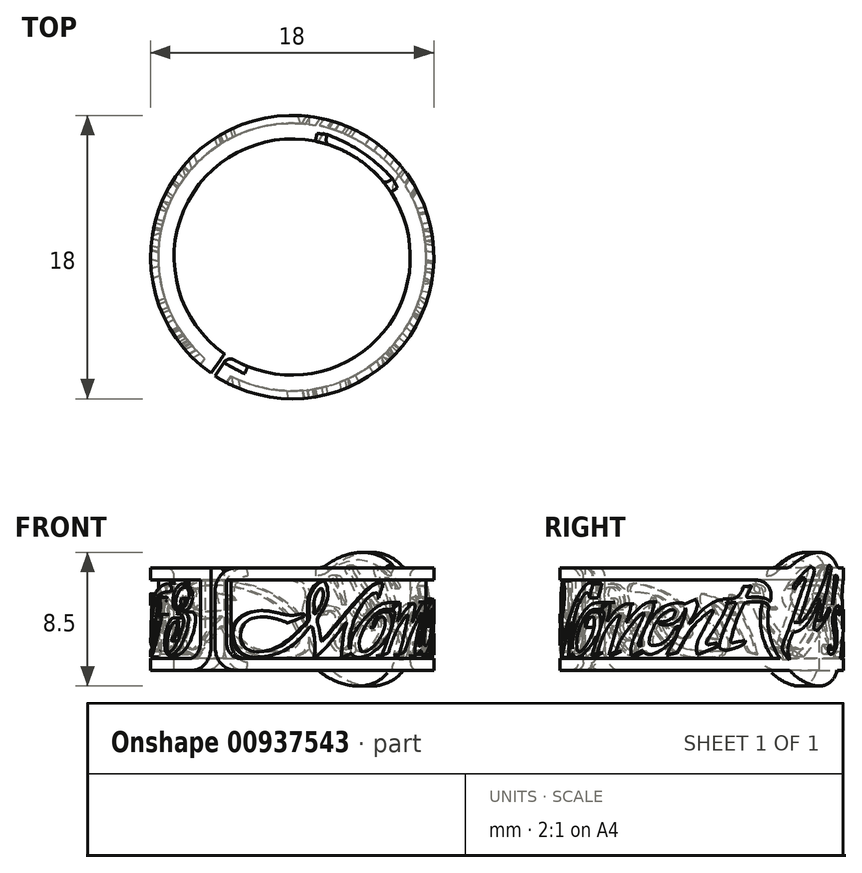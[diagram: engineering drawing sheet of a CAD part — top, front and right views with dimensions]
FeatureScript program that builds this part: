
annotation { "Feature Type Name" : "Feature", "Feature Type Description" : "" }
export const myFeature = defineFeature(function(context is Context, id is Id, definition is map)
    precondition{}
    {
        {
            var Q0;
            Q0=qCreatedBy(makeId("Top.planeOp"),FACE);
            var sketch = newSketch(context, id + "F0", { "sketchPlane" : qUnion([Q0])});
            skCircle(sketch, "E0", {"center": v(0, 0) * mm, "radius": 8.5 * mm});
            skSolve(sketch);
        }
        {
            var Q0;
            Q0 = qSketchRegion(id + "F0", true);
            extrude(context, id + "F1", {"entities" : qUnion([Q0]), "depth" : 5 * mm, "offsetDistance" : 25 * mm});
        }
        {
            var Q0;
            Q0=qCreatedBy(makeId("Top.planeOp"),FACE);
            var sketch = newSketch(context, id + "F2", { "sketchPlane" : qUnion([Q0])});
            skCircle(sketch, "E1.cCircle", {"center": v(0, 0) * mm, "radius": 28.24 * mm, "construction": true});
            skLineSegment(sketch, "E1.0", {"start": v(23.72, -15.98) * mm, "end": v(17.62, -22.52) * mm});
            skLineSegment(sketch, "E1.1", {"start": v(17.62, -22.52) * mm, "end": v(9.8, -26.86) * mm});
            skLineSegment(sketch, "E1.2", {"start": v(9.8, -26.86) * mm, "end": v(1.02, -28.58) * mm});
            skLineSegment(sketch, "E1.3", {"start": v(1.02, -28.58) * mm, "end": v(-7.86, -27.5) * mm});
            skLineSegment(sketch, "E1.4", {"start": v(-7.86, -27.5) * mm, "end": v(-15.98, -23.72) * mm});
            skLineSegment(sketch, "E1.5", {"start": v(-15.98, -23.72) * mm, "end": v(-22.52, -17.62) * mm});
            skLineSegment(sketch, "E1.6", {"start": v(-22.52, -17.62) * mm, "end": v(-26.86, -9.8) * mm});
            skLineSegment(sketch, "E1.7", {"start": v(-26.86, -9.8) * mm, "end": v(-28.58, -1.02) * mm});
            skLineSegment(sketch, "E1.8", {"start": v(-28.58, -1.02) * mm, "end": v(-27.5, 7.86) * mm});
            skLineSegment(sketch, "E1.9", {"start": v(-27.5, 7.86) * mm, "end": v(-23.72, 15.98) * mm});
            skLineSegment(sketch, "E1.10", {"start": v(-23.72, 15.98) * mm, "end": v(-17.62, 22.52) * mm});
            skLineSegment(sketch, "E1.11", {"start": v(-17.62, 22.52) * mm, "end": v(-9.8, 26.86) * mm});
            skLineSegment(sketch, "E1.12", {"start": v(-9.8, 26.86) * mm, "end": v(-1.02, 28.58) * mm});
            skLineSegment(sketch, "E1.13", {"start": v(-1.02, 28.58) * mm, "end": v(7.86, 27.5) * mm});
            skLineSegment(sketch, "E1.14", {"start": v(7.86, 27.5) * mm, "end": v(15.98, 23.72) * mm});
            skLineSegment(sketch, "E1.15", {"start": v(15.98, 23.72) * mm, "end": v(22.52, 17.62) * mm});
            skLineSegment(sketch, "E1.16", {"start": v(22.52, 17.62) * mm, "end": v(26.86, 9.8) * mm});
            skLineSegment(sketch, "E1.17", {"start": v(26.86, 9.8) * mm, "end": v(28.58, 1.02) * mm});
            skLineSegment(sketch, "E1.18", {"start": v(28.58, 1.02) * mm, "end": v(27.5, -7.86) * mm});
            skLineSegment(sketch, "E1.19", {"start": v(27.5, -7.86) * mm, "end": v(23.72, -15.98) * mm});
            skPoint(sketch, "E1.0.midPoint", {"position": v(20.67, -19.25) * mm});
            skLineSegment(sketch, "E2", {"start": v(-15.98, -23.72) * mm, "end": v(15.98, 23.72) * mm, "construction": true});
            skLineSegment(sketch, "E3", {"start": v(0, 0) * mm, "end": v(22.52, 17.62) * mm, "construction": true});
            skLineSegment(sketch, "E4", {"start": v(0, 0) * mm, "end": v(7.86, 27.5) * mm, "construction": true});
            skLineSegment(sketch, "E5", {"start": v(-23.72, 15.98) * mm, "end": v(-28.58, -1.02) * mm});
            skLineSegment(sketch, "E6", {"start": v(-28.58, -1.02) * mm, "end": v(-22.52, -17.62) * mm});
            skLineSegment(sketch, "E7", {"start": v(-1.02, 28.58) * mm, "end": v(-17.62, 22.52) * mm});
            skLineSegment(sketch, "E8", {"start": v(7.86, 27.5) * mm, "end": v(22.52, 17.62) * mm});
            skLineSegment(sketch, "E9", {"start": v(-7.86, -27.5) * mm, "end": v(-22.52, -17.62) * mm});
            skSolve(sketch);
        }
        {
            var Q0;
            Q0=sQuery(id+"F2.wireOp",EDGE,"E1.2");
            var Q1;
            Q1=sQuery(id+"F2.wireOp",VERTEX,"E1.cCircle.center");
            cPlane(context, id + "F3", {"entities" : qUnion([Q0, Q1]), "cplaneType" : CPlaneType.LINE_ANGLE, "offset" : 25 * mm, "angle" : 90 * degree, "width" : 150 * mm, "height" : 150 * mm});
        }
        {
            var Q0;
            Q0=sQuery(id+"F2.wireOp",EDGE,"E1.1");
            var Q1;
            Q1=sQuery(id+"F2.wireOp",VERTEX,"E1.cCircle.center");
            cPlane(context, id + "F4", {"entities" : qUnion([Q0, Q1]), "cplaneType" : CPlaneType.LINE_ANGLE, "offset" : 25 * mm, "angle" : 90 * degree, "width" : 150 * mm, "height" : 150 * mm});
        }
        {
            var Q0;
            Q0=sQuery(id+"F2.wireOp",EDGE,"E1.0");
            var Q1;
            Q1=sQuery(id+"F2.wireOp",VERTEX,"E1.cCircle.center");
            cPlane(context, id + "F5", {"entities" : qUnion([Q0, Q1]), "cplaneType" : CPlaneType.LINE_ANGLE, "offset" : 25 * mm, "angle" : 90 * degree, "width" : 150 * mm, "height" : 150 * mm});
        }
        {
            var Q0;
            Q0=sQuery(id+"F2.wireOp",EDGE,"E1.19");
            var Q1;
            Q1=sQuery(id+"F2.wireOp",VERTEX,"E1.cCircle.center");
            cPlane(context, id + "F6", {"entities" : qUnion([Q0, Q1]), "cplaneType" : CPlaneType.LINE_ANGLE, "offset" : 25 * mm, "angle" : 90 * degree, "width" : 150 * mm, "height" : 150 * mm});
        }
        {
            var Q0;
            Q0=sQuery(id+"F2.wireOp",EDGE,"E1.18");
            var Q1;
            Q1=sQuery(id+"F2.wireOp",VERTEX,"E1.cCircle.center");
            cPlane(context, id + "F7", {"entities" : qUnion([Q0, Q1]), "cplaneType" : CPlaneType.LINE_ANGLE, "offset" : 25 * mm, "angle" : 90 * degree, "width" : 150 * mm, "height" : 150 * mm});
        }
        {
            var Q0;
            Q0=qCreatedBy(id+"F3.planeOp",FACE);
            var sketch = newSketch(context, id + "F8", { "sketchPlane" : qUnion([Q0])});
            skLineSegment(sketch, "E10", {"start": v(4.04, 3.86) * mm, "end": v(4.36, 4.75) * mm});
            skLineSegment(sketch, "E11", {"start": v(1.44, 0.05) * mm, "end": v(2.31, 0.4) * mm});
            skLineSegment(sketch, "E12", {"start": v(-2, 2.27) * mm, "end": v(-1, 2.66) * mm});
            skFitSpline(sketch, "E13", {"points": [v(4.36, 4.75) * mm, v(3.51, 4.55) * mm, v(0.18, 1.08) * mm, v(0.15, 1.1) * mm, v(0, 1.84) * mm, v(-0.12, 2.5) * mm, v(0.43, 3.47) * mm, v(0.51, 4.56) * mm, v(0.25, 4.94) * mm, v(-0.33, 4.49) * mm, v(-0.66, 3.57) * mm, v(-0.64, 2.43) * mm, v(-0.65, 2.41) * mm, v(-2.42, 0.81) * mm, v(-4.49, 0.63) * mm, v(-4.82, 1.53) * mm, v(-4.47, 2.36) * mm, v(-3.44, 2.64) * mm, v(-2, 2.27) * mm], "startDerivative": vector(-10.65, 3.61) * mm, "endDerivative": vector(19.15, -8.06) * mm});
            skFitSpline(sketch, "E14", {"points": [v(4.04, 3.86) * mm, v(3.9, 4.15) * mm, v(3.51, 4.05) * mm, v(2.35, 2.53) * mm, v(1.98, 0.7) * mm, v(2.06, 0.63) * mm, v(2.4, 0.63) * mm, v(2.55, 0.5) * mm, v(2.31, 0.4) * mm], "startDerivative": vector(-0.87, 3.73) * mm, "endDerivative": vector(-2.87, -1.15) * mm});
            skPoint(sketch, "E15.8.internal.snap0", {"position": v(1.87, 0.23) * mm});
            skFitSpline(sketch, "E15", {"points": [v(1.43, 0) * mm, v(1.54, 1.1) * mm, v(1.73, 2.1) * mm, v(1.8, 2.29) * mm, v(1.78, 2.3) * mm, v(1.26, 1.67) * mm, v(-0.3, 0.09) * mm, v(-0.36, 0.12) * mm, v(-0.32, 0.23) * mm, v(-0.33, 1.4) * mm, v(-0.5, 2.04) * mm, v(-0.74, 1.84) * mm, v(-2, 0.64) * mm, v(-3.8, 0.09) * mm, v(-4.76, 0.36) * mm, v(-5.24, 1.53) * mm, v(-4.78, 2.62) * mm, v(-3.38, 3.04) * mm, v(-1.8, 2.75) * mm, v(-1.08, 2.84) * mm, v(-0.96, 2.8) * mm, v(-1, 2.66) * mm], "startDerivative": vector(1.9, 19.1) * mm, "endDerivative": vector(-4.87, -6.02) * mm});
            skFitSpline(sketch, "E16", {"points": [v(-0.3, 2.83) * mm, v(0.15, 3.55) * mm, v(0.23, 4.32) * mm, v(0.09, 4.44) * mm, v(-0.3, 3.8) * mm, v(-0.32, 3.14) * mm, v(-0.3, 2.83) * mm]});
            skSolve(sketch);
        }
        {
            var Q0;
            Q0=makeQuery(id+"F8.imprint","IMPRINT",FACE,{"disambiguationData":[TD([[makeQuery(id+"F8.imprint","IMPRINT",EDGE,{"derivedFrom":sQuery(id+"F8.wireOp",EDGE,"E10")}),1.0]])]});
            extrude(context, id + "F9", {"entities" : qUnion([Q0]), "operationType" : NewBodyOperationType.ADD, "oppositeDirection" : true, "depth" : 25 * mm, "offsetDistance" : 25 * mm});
        }
        {
            var Q0;
            Q0=makeQuery(id+"F1.opExtrude","CAP_FACE",FACE,{"disambiguationData":[OSD([sQuery(id+"F0.wireOp",EDGE,"E0")])],"isStart":false});
            var sketch = newSketch(context, id + "F10", { "sketchPlane" : qUnion([Q0])});
            skCircle(sketch, "E17", {"center": v(0, 0) * mm, "radius": 9 * mm});
            skCircle(sketch, "E18", {"center": v(0, 0) * mm, "radius": 7.5 * mm});
            skSolve(sketch);
        }
        {
            var Q0;
            Q0=qCreatedBy(id+"F4.planeOp",FACE);
            var sketch = newSketch(context, id + "F11", { "sketchPlane" : qUnion([Q0])});
            skLineSegment(sketch, "E19", {"start": v(2.5, 3.11) * mm, "end": v(2.64, 3.57) * mm});
            skFitSpline(sketch, "E20", {"points": [v(2.64, 3.57) * mm, v(1.55, 3.43) * mm, v(0.12, 2.4) * mm, v(-0.67, 1.2) * mm, v(-0.64, 0.27) * mm, v(0.15, 0.1) * mm, v(1.44, 0.79) * mm, v(2.37, 1.93) * mm, v(2.3, 2.85) * mm, v(1.85, 2.96) * mm, v(1.29, 2.77) * mm, v(0.94, 2.22) * mm, v(0.94, 2) * mm, v(0.97, 1.98) * mm, v(1.13, 2.27) * mm, v(1.52, 2.62) * mm, v(1.8, 2.56) * mm, v(1.83, 2.08) * mm, v(1.26, 1.08) * mm, v(0.2, 0.42) * mm, v(-0.1, 0.7) * mm, v(-0.02, 1.45) * mm, v(0.6, 2.4) * mm, v(1.56, 3.07) * mm, v(2.5, 3.11) * mm], "startDerivative": vector(-21.3, 0.4) * mm, "endDerivative": vector(20.6, -1.62) * mm});
            skSolve(sketch);
        }
        {
            var Q0;
            Q0 = qSketchRegion(id + "F11", true);
            var Q1;
            Q1=makeQuery(id+"F1.opExtrude","SWEPT_BODY",BODY,{"disambiguationData":[OSD([sQuery(id+"F0.wireOp",EDGE,"E0")])]});
            extrude(context, id + "F12", {"entities" : qUnion([Q0]), "operationType" : NewBodyOperationType.ADD, "endBound" : BoundingType.UP_TO_BODY, "oppositeDirection" : true, "depth" : 25 * mm, "endBoundEntityBody" : qUnion([Q1]), "offsetDistance" : 25 * mm});
        }
        {
            var Q0;
            Q0=qCreatedBy(id+"F5.planeOp",FACE);
            var sketch = newSketch(context, id + "F13", { "sketchPlane" : qUnion([Q0])});
            skLineSegment(sketch, "E21", {"start": v(-1.23, 0.17) * mm, "end": v(-0.68, 0.37) * mm});
            skLineSegment(sketch, "E22", {"start": v(0.33, 0.24) * mm, "end": v(0.9, 0.45) * mm});
            skLineSegment(sketch, "E23", {"start": v(2.03, 0.16) * mm, "end": v(2.91, 0.57) * mm});
            skLineSegment(sketch, "E24", {"start": v(-0.43, 3.05) * mm, "end": v(0.39, 3.56) * mm});
            skFitSpline(sketch, "E25", {"points": [v(-0.43, 3.05) * mm, v(-0.13, 2.97) * mm, v(-0.1, 2.74) * mm, v(-1.23, 0.17) * mm], "startDerivative": vector(1.74, -0.24) * mm, "endDerivative": vector(-2.5, -5.21) * mm});
            skFitSpline(sketch, "E26", {"points": [v(-0.68, 0.37) * mm, v(-0.05, 1.6) * mm, v(0.97, 2.67) * mm, v(1.24, 2.75) * mm, v(1.2, 2.63) * mm, v(0.86, 1.65) * mm, v(0.33, 0.24) * mm], "startDerivative": vector(2.52, 5.6) * mm, "endDerivative": vector(-2.42, -5.93) * mm});
            skFitSpline(sketch, "E27", {"points": [v(0.39, 3.56) * mm, v(0.39, 3.05) * mm, v(0.16, 2.4) * mm, v(0.16, 2.36) * mm, v(0.79, 2.95) * mm, v(1.77, 3.48) * mm, v(2, 3.43) * mm, v(2.02, 3.28) * mm, v(1.78, 2.52) * mm, v(1.68, 2.3) * mm, v(1.68, 2.27) * mm, v(2.23, 2.86) * mm, v(3.19, 3.56) * mm, v(3.52, 3.56) * mm, v(3.56, 3.32) * mm, v(3.06, 2.07) * mm, v(2.58, 1.06) * mm, v(2.52, 0.87) * mm, v(2.77, 0.77) * mm, v(2.9, 0.77) * mm, v(2.91, 0.57) * mm], "startDerivative": vector(1.22, -8.4) * mm, "endDerivative": vector(-1.27, -5.43) * mm});
            skFitSpline(sketch, "E28", {"points": [v(2.03, 0.16) * mm, v(2.03, 0.57) * mm, v(2.37, 1.6) * mm, v(2.91, 2.8) * mm, v(2.91, 2.93) * mm, v(2.91, 2.94) * mm, v(2.83, 2.9) * mm, v(1.72, 1.74) * mm, v(0.9, 0.45) * mm], "startDerivative": vector(-0.3, 3.7) * mm, "endDerivative": vector(-2.66, -6.56) * mm});
            skSolve(sketch);
        }
        {
            var Q0;
            Q0 = qSketchRegion(id + "F13", true);
            var Q1;
            Q1=makeQuery(id+"F1.opExtrude","SWEPT_BODY",BODY,{"disambiguationData":[OSD([sQuery(id+"F0.wireOp",EDGE,"E0")])]});
            extrude(context, id + "F14", {"entities" : qUnion([Q0]), "operationType" : NewBodyOperationType.ADD, "endBound" : BoundingType.UP_TO_BODY, "oppositeDirection" : true, "depth" : 25 * mm, "endBoundEntityBody" : qUnion([Q1]), "offsetDistance" : 25 * mm});
        }
        {
            var Q0;
            Q0=qCreatedBy(id+"F6.planeOp",FACE);
            var sketch = newSketch(context, id + "F15", { "sketchPlane" : qUnion([Q0])});
            skFitSpline(sketch, "E29", {"points": [v(2.3, 2.05) * mm, v(2.36, 1.72) * mm, v(2.04, 1.13) * mm, v(0.9, 0.34) * mm, v(0.17, 0.36) * mm, v(-0.06, 0.94) * mm, v(0.34, 2.1) * mm, v(1.52, 3.31) * mm, v(2.56, 3.54) * mm, v(2.8, 3.44) * mm, v(2.83, 3.16) * mm, v(2.38, 2.43) * mm, v(1.71, 2.14) * mm, v(1.17, 2.22) * mm, v(1.16, 2.3) * mm, v(1.53, 2.35) * mm, v(2.15, 2.72) * mm, v(2.19, 3.04) * mm, v(1.88, 3.07) * mm, v(1.4, 2.8) * mm, v(0.83, 2.04) * mm, v(0.54, 0.93) * mm, v(0.94, 0.83) * mm, v(1.44, 1.01) * mm, v(1.93, 1.49) * mm, v(2.3, 2.05) * mm]});
            skSolve(sketch);
        }
        {
            var Q0;
            Q0 = qSketchRegion(id + "F15", true);
            var Q1;
            Q1=makeQuery(id+"F1.opExtrude","SWEPT_BODY",BODY,{"disambiguationData":[OSD([sQuery(id+"F0.wireOp",EDGE,"E0")])]});
            extrude(context, id + "F16", {"entities" : qUnion([Q0]), "operationType" : NewBodyOperationType.ADD, "endBound" : BoundingType.UP_TO_BODY, "oppositeDirection" : true, "depth" : 25 * mm, "endBoundEntityBody" : qUnion([Q1]), "offsetDistance" : 25 * mm});
        }
        {
            var Q0;
            Q0=qCreatedBy(id+"F7.planeOp",FACE);
            var sketch = newSketch(context, id + "F17", { "sketchPlane" : qUnion([Q0])});
            skLineSegment(sketch, "E30", {"start": v(0.82, 0.24) * mm, "end": v(2.03, 0.72) * mm});
            skLineSegment(sketch, "E31", {"start": v(-0.28, 3.33) * mm, "end": v(0.69, 3.75) * mm});
            skLineSegment(sketch, "E32", {"start": v(-1.15, 0.23) * mm, "end": v(-0.5, 0.37) * mm});
            skFitSpline(sketch, "E33", {"points": [v(-0.28, 3.33) * mm, v(-0.28, 3.24) * mm, v(0, 3.26) * mm, v(0.09, 2.97) * mm, v(-0.68, 1.1) * mm, v(-1.15, 0.23) * mm], "startDerivative": vector(-0.42, -1.38) * mm, "endDerivative": vector(-1.12, -2.15) * mm});
            skFitSpline(sketch, "E34", {"points": [v(-0.5, 0.37) * mm, v(0.25, 1.66) * mm, v(1, 2.48) * mm, v(1.72, 3.05) * mm, v(1.82, 3.07) * mm, v(1.82, 3.02) * mm, v(1.2, 1.8) * mm, v(0.78, 0.79) * mm, v(0.82, 0.24) * mm], "startDerivative": vector(4.05, 6.46) * mm, "endDerivative": vector(0.54, -3.79) * mm});
            skFitSpline(sketch, "E35", {"points": [v(2.03, 0.72) * mm, v(2.03, 0.95) * mm, v(2.03, 0.98) * mm, v(1.8, 0.94) * mm, v(1.44, 0.88) * mm, v(1.39, 1) * mm, v(1.64, 1.46) * mm, v(2.6, 3.18) * mm, v(2.61, 3.61) * mm, v(2.38, 3.72) * mm, v(2.03, 3.65) * mm, v(1.1, 3.04) * mm, v(0.3, 2.18) * mm, v(0.3, 2.2) * mm, v(0.6, 2.76) * mm, v(0.82, 3.49) * mm, v(0.69, 3.75) * mm], "startDerivative": vector(-0.17, 3.4) * mm, "endDerivative": vector(-2.57, 4.39) * mm});
            skSolve(sketch);
        }
        {
            var Q0;
            Q0 = qSketchRegion(id + "F17", true);
            var Q1;
            Q1=makeQuery(id+"F1.opExtrude","SWEPT_BODY",BODY,{"disambiguationData":[OSD([sQuery(id+"F0.wireOp",EDGE,"E0")])]});
            extrude(context, id + "F18", {"entities" : qUnion([Q0]), "operationType" : NewBodyOperationType.ADD, "endBound" : BoundingType.UP_TO_BODY, "oppositeDirection" : true, "depth" : 25 * mm, "endBoundEntityBody" : qUnion([Q1]), "offsetDistance" : 25 * mm});
        }
        {
            var Q0;
            Q0=sQuery(id+"F2.wireOp",EDGE,"E1.17");
            var Q1;
            Q1=sQuery(id+"F2.wireOp",VERTEX,"E1.cCircle.center");
            cPlane(context, id + "F19", {"entities" : qUnion([Q0, Q1]), "cplaneType" : CPlaneType.LINE_ANGLE, "offset" : 25 * mm, "angle" : 90 * degree, "width" : 150 * mm, "height" : 150 * mm});
        }
        {
            var Q0;
            Q0=qCreatedBy(id+"F19.planeOp",FACE);
            var sketch = newSketch(context, id + "F20", { "sketchPlane" : qUnion([Q0])});
            skFitSpline(sketch, "E36", {"points": [v(1, 0.94) * mm, v(0.26, 0.62) * mm, v(-0.26, 0.53) * mm, v(-0.54, 0.65) * mm, v(-0.6, 0.94) * mm, v(0.16, 2.87) * mm, v(0.49, 3.5) * mm, v(0.5, 3.56) * mm, v(-0.03, 3.56) * mm, v(-0.37, 3.74) * mm, v(-0.35, 3.78) * mm, v(-0.03, 3.79) * mm, v(0.43, 3.84) * mm, v(0.77, 4.13) * mm, v(0.98, 4.55) * mm, v(1, 4.59) * mm, v(1.26, 4.59) * mm, v(1.48, 4.62) * mm, v(1.49, 4.59) * mm, v(1.31, 4.22) * mm, v(1.18, 3.9) * mm, v(1.22, 3.88) * mm, v(1.5, 3.9) * mm, v(2.11, 3.88) * mm, v(2.9, 3.45) * mm, v(2.74, 3) * mm, v(2.65, 3.36) * mm, v(2.17, 3.59) * mm, v(1.37, 3.6) * mm, v(1.02, 3.55) * mm, v(0.99, 3.48) * mm, v(0.57, 2.55) * mm, v(0.18, 1.32) * mm, v(0.15, 1) * mm, v(0.54, 1.06) * mm, v(1.01, 1.13) * mm, v(1.1, 1.14) * mm, v(1, 0.94) * mm]});
            skSolve(sketch);
        }
        {
            var Q0;
            Q0 = qSketchRegion(id + "F20", true);
            var Q1;
            Q1=makeQuery(id+"F1.opExtrude","SWEPT_BODY",BODY,{"disambiguationData":[OSD([sQuery(id+"F0.wireOp",EDGE,"E0")])]});
            extrude(context, id + "F21", {"entities" : qUnion([Q0]), "operationType" : NewBodyOperationType.ADD, "endBound" : BoundingType.UP_TO_BODY, "oppositeDirection" : true, "depth" : 25 * mm, "endBoundEntityBody" : qUnion([Q1]), "offsetDistance" : 25 * mm});
        }
        {
            var Q0;
            Q0=sQuery(id+"F2.wireOp",EDGE,"E6");
            cPlane(context, id + "F22", {"entities" : qUnion([Q0]), "cplaneType" : CPlaneType.LINE_ANGLE, "offset" : 25 * mm, "angle" : 90 * degree, "oppositeDirection" : true, "width" : 150 * mm, "height" : 150 * mm});
        }
        {
            var Q0;
            Q0=qCreatedBy(id+"F22.planeOp",FACE);
            var sketch = newSketch(context, id + "F23", { "sketchPlane" : qUnion([Q0])});
            skFitSpline(sketch, "E37", {"points": [v(0.11, 3.88) * mm, v(0.03, 3.86) * mm, v(-0.58, 2.73) * mm, v(-1.28, 1.98) * mm, v(-1.7, 1.93) * mm, v(-1.7, 2.58) * mm, v(-0.58, 3.8) * mm, v(0.92, 4.21) * mm, v(1.63, 4.25) * mm, v(1.84, 4.33) * mm, v(1.67, 4.67) * mm, v(1.37, 4.77) * mm, v(-0.04, 4.44) * mm, v(-1.54, 3.63) * mm, v(-2.18, 2.5) * mm, v(-2.33, 1.44) * mm, v(-1.6, 1.38) * mm, v(-0.38, 2.37) * mm, v(-0.32, 2.37) * mm, v(-1.07, 1.16) * mm, v(-3.15, 0.45) * mm, v(-4.2, 0.49) * mm, v(-4.3, 0.5) * mm, v(-4.32, 0.49) * mm, v(-4.28, 0.3) * mm, v(-3.1, 0.1) * mm, v(-1.74, 0.27) * mm, v(-0.51, 1.17) * mm, v(0.49, 2.77) * mm, v(0.46, 2.8) * mm, v(-0.07, 2.62) * mm, v(-0.1, 2.62) * mm, v(0.27, 3.2) * mm, v(0.29, 3.29) * mm, v(0.11, 3.88) * mm]});
            skSolve(sketch);
        }
        {
            var Q0;
            Q0 = qSketchRegion(id + "F23", true);
            var Q1;
            Q1=makeQuery(id+"F1.opExtrude","SWEPT_BODY",BODY,{"disambiguationData":[OSD([sQuery(id+"F0.wireOp",EDGE,"E0")])]});
            extrude(context, id + "F24", {"entities" : qUnion([Q0]), "operationType" : NewBodyOperationType.ADD, "oppositeDirection" : true, "depth" : 25 * mm, "endBoundEntityBody" : qUnion([Q1]), "offsetDistance" : 25 * mm});
        }
        {
            var Q0;
            Q0=sQuery(id+"F2.wireOp",EDGE,"E5");
            var Q1;
            Q1=sQuery(id+"F2.wireOp",VERTEX,"E3.start");
            cPlane(context, id + "F25", {"entities" : qUnion([Q0, Q1]), "cplaneType" : CPlaneType.LINE_ANGLE, "offset" : 25 * mm, "angle" : 90 * degree, "width" : 150 * mm, "height" : 150 * mm});
        }
        {
            var Q0;
            Q0=qCreatedBy(id+"F25.planeOp",FACE);
            var sketch = newSketch(context, id + "F26", { "sketchPlane" : qUnion([Q0])});
            skLineSegment(sketch, "E38", {"start": v(0.74, 0.59) * mm, "end": v(2.02, 1.02) * mm});
            skLineSegment(sketch, "E39", {"start": v(-1.16, 0.27) * mm, "end": v(-0.58, 0.44) * mm});
            skLineSegment(sketch, "E40", {"start": v(-0.58, 3.65) * mm, "end": v(0.58, 4.08) * mm});
            skFitSpline(sketch, "E41", {"points": [v(-0.58, 3.65) * mm, v(-0.58, 3.44) * mm, v(-0.27, 3.55) * mm, v(-0.03, 3.57) * mm, v(0.03, 3.4) * mm, v(-0.78, 1.5) * mm, v(-1.16, 0.27) * mm], "startDerivative": vector(-0.28, -1.42) * mm, "endDerivative": vector(-1.17, -2.68) * mm});
            skFitSpline(sketch, "E42", {"points": [v(-0.58, 0.44) * mm, v(0.19, 2.04) * mm, v(1.1, 2.99) * mm, v(1.7, 3.49) * mm, v(1.75, 3.5) * mm, v(1.73, 3.4) * mm, v(1.07, 2.08) * mm, v(0.66, 0.86) * mm, v(0.74, 0.59) * mm], "startDerivative": vector(3.64, 6.49) * mm, "endDerivative": vector(0.84, -1.9) * mm});
            skFitSpline(sketch, "E43", {"points": [v(2.02, 1.02) * mm, v(2.02, 1.23) * mm, v(2.02, 1.3) * mm, v(2.02, 1.31) * mm, v(1.43, 1.21) * mm, v(1.3, 1.26) * mm, v(1.82, 2.24) * mm, v(2.55, 3.58) * mm, v(2.56, 4) * mm, v(2.46, 4.1) * mm, v(2.02, 4.03) * mm, v(1.05, 3.49) * mm, v(0.37, 2.77) * mm, v(0.31, 2.74) * mm, v(0.31, 2.87) * mm, v(0.6, 3.46) * mm, v(0.58, 4.08) * mm], "startDerivative": vector(3.58, 2.62) * mm, "endDerivative": vector(-1.5, 7.9) * mm});
            skSolve(sketch);
        }
        {
            var Q0;
            Q0 = qSketchRegion(id + "F26", true);
            var Q1;
            Q1=makeQuery(id+"F1.opExtrude","SWEPT_BODY",BODY,{"disambiguationData":[OSD([sQuery(id+"F0.wireOp",EDGE,"E0")])]});
            extrude(context, id + "F27", {"entities" : qUnion([Q0]), "operationType" : NewBodyOperationType.ADD, "endBound" : BoundingType.UP_TO_BODY, "oppositeDirection" : true, "depth" : 25 * mm, "endBoundEntityBody" : qUnion([Q1]), "offsetDistance" : 25 * mm});
        }
        {
            var Q0;
            Q0=sQuery(id+"F2.wireOp",EDGE,"E1.10");
            cPlane(context, id + "F28", {"entities" : qUnion([Q0]), "cplaneType" : CPlaneType.LINE_ANGLE, "offset" : 25 * mm, "angle" : 90 * degree, "oppositeDirection" : true, "width" : 150 * mm, "height" : 150 * mm});
        }
        {
            var Q0;
            Q0=qCreatedBy(id+"F28.planeOp",FACE);
            var sketch = newSketch(context, id + "F29", { "sketchPlane" : qUnion([Q0])});
            skLineSegment(sketch, "E44", {"start": v(0.56, 0.25) * mm, "end": v(1.52, 0.5) * mm});
            skLineSegment(sketch, "E45", {"start": v(1.76, 3.3) * mm, "end": v(3, 3.8) * mm});
            skFitSpline(sketch, "E46", {"points": [v(3, 3.8) * mm, v(2.76, 2.8) * mm, v(1.64, 1.3) * mm, v(1.04, 0.72) * mm, v(1.05, 0.67) * mm, v(1.52, 0.73) * mm, v(1.73, 0.73) * mm, v(1.76, 0.67) * mm, v(1.52, 0.5) * mm], "startDerivative": vector(-0.48, -5.2) * mm, "endDerivative": vector(-4.13, -1.64) * mm});
            skFitSpline(sketch, "E47", {"points": [v(0.56, 0.25) * mm, v(0.56, 0.73) * mm, v(1.87, 2.12) * mm, v(2.35, 3.23) * mm, v(2.3, 3.3) * mm, v(2.1, 3.25) * mm, v(1.68, 3.14) * mm, v(1.76, 3.3) * mm], "startDerivative": vector(-2.62, 1.33) * mm, "endDerivative": vector(1.96, 2.42) * mm});
            skFitSpline(sketch, "E48", {"points": [v(3, 4.7) * mm, v(3.23, 4.55) * mm, v(3.15, 4.24) * mm, v(2.63, 4.17) * mm, v(2.54, 4.45) * mm, v(3, 4.7) * mm]});
            skSolve(sketch);
        }
        {
            var Q0;
            Q0 = qSketchRegion(id + "F29", true);
            extrude(context, id + "F30", {"entities" : qUnion([Q0]), "operationType" : NewBodyOperationType.ADD, "oppositeDirection" : true, "depth" : 21 * mm, "offsetDistance" : 25 * mm});
        }
        {
            var Q0;
            Q0=sQuery(id+"F2.wireOp",EDGE,"E7");
            var Q1;
            Q1=sQuery(id+"F2.wireOp",VERTEX,"E3.start");
            cPlane(context, id + "F31", {"entities" : qUnion([Q0, Q1]), "cplaneType" : CPlaneType.LINE_ANGLE, "offset" : 25 * mm, "angle" : 90 * degree, "width" : 150 * mm, "height" : 150 * mm});
        }
        {
            var Q0;
            Q0=qCreatedBy(id+"F31.planeOp",FACE);
            var sketch = newSketch(context, id + "F32", { "sketchPlane" : qUnion([Q0])});
            skLineSegment(sketch, "E49", {"start": v(2.02, 4.16) * mm, "end": v(0.92, 3.96) * mm});
            skLineSegment(sketch, "E50", {"start": v(3.62, 0.13) * mm, "end": v(4.52, 0.55) * mm});
            skFitSpline(sketch, "E51", {"points": [v(4.52, 0.55) * mm, v(4.52, 0.63) * mm, v(4.24, 0.69) * mm, v(3.84, 0.57) * mm, v(2.85, 1.47) * mm, v(1.2, 2.9) * mm, v(-0.2, 3.01) * mm, v(-0.98, 2.73) * mm, v(-1.6, 1.87) * mm, v(-1.44, 1.48) * mm, v(-1.39, 1.5) * mm, v(-1.36, 1.9) * mm, v(-0.54, 2.57) * mm, v(0.46, 2.62) * mm, v(1.1, 2.42) * mm, v(2.7, 0.98) * mm, v(3.62, 0.13) * mm], "startDerivative": vector(1.06, 5.25) * mm, "endDerivative": vector(10.2, -9.08) * mm});
            skFitSpline(sketch, "E52", {"points": [v(2.02, 4.16) * mm, v(1.92, 3.54) * mm, v(1.77, 3.08) * mm, v(1.79, 3.07) * mm, v(2.95, 3.02) * mm, v(3.95, 3.45) * mm, v(3.97, 4.12) * mm, v(3.13, 4.56) * mm, v(1.18, 4.6) * mm, v(-1.36, 3.85) * mm, v(-3.2, 2.1) * mm, v(-3.21, 0.78) * mm, v(-1.18, 0.52) * mm, v(0.64, 1.58) * mm, v(1.28, 3.36) * mm, v(1.28, 3.74) * mm, v(1.22, 3.77) * mm, v(0.77, 3.7) * mm, v(0.72, 3.7) * mm, v(0.92, 3.96) * mm], "startDerivative": vector(3.16, -11.36) * mm, "endDerivative": vector(7.72, 6.07) * mm});
            skFitSpline(sketch, "E53", {"points": [v(1.71, 2.7) * mm, v(3.1, 2.52) * mm, v(3.12, 2.57) * mm, v(3.52, 2.87) * mm, v(4.4, 3.29) * mm, v(4.52, 4.3) * mm, v(2.99, 4.9) * mm, v(0.82, 4.85) * mm, v(-1.73, 4.12) * mm, v(-3.82, 2.2) * mm, v(-4.05, 1.05) * mm, v(-3.53, 0.3) * mm, v(-1.26, 0.13) * mm, v(0.3, 0.66) * mm, v(1.43, 1.7) * mm, v(1.73, 2.66) * mm, v(1.71, 2.7) * mm]});
            skSolve(sketch);
        }
        {
            var Q0;
            Q0 = qSketchRegion(id + "F32", true);
            var Q1;
            Q1=makeQuery(id+"F1.opExtrude","SWEPT_BODY",BODY,{"disambiguationData":[OSD([sQuery(id+"F0.wireOp",EDGE,"E0")])]});
            extrude(context, id + "F33", {"entities" : qUnion([Q0]), "operationType" : NewBodyOperationType.ADD, "oppositeDirection" : true, "depth" : 25 * mm, "endBoundEntityBody" : qUnion([Q1]), "offsetDistance" : 25 * mm});
        }
        {
            var Q0;
            Q0=sQuery(id+"F2.wireOp",EDGE,"E8");
            var Q1;
            Q1=sQuery(id+"F2.wireOp",VERTEX,"E3.start");
            cPlane(context, id + "F34", {"entities" : qUnion([Q0, Q1]), "cplaneType" : CPlaneType.LINE_ANGLE, "offset" : 25 * mm, "angle" : 90 * degree, "width" : 150 * mm, "height" : 150 * mm});
        }
        {
            var Q0;
            Q0=qCreatedBy(id+"F34.planeOp",FACE);
            var sketch = newSketch(context, id + "F35", { "sketchPlane" : qUnion([Q0])});
            skFitSpline(sketch, "E54", {"points": [v(-3.35, 4.7) * mm, v(-2.78, 5.18) * mm, v(-2.34, 5.42) * mm, v(-2.2, 5.42) * mm, v(-2.17, 5.35) * mm, v(-2.2, 5.26) * mm, v(-4.18, 1.66) * mm, v(-5.36, -0.62) * mm, v(-5.72, -1.46) * mm, v(-5.72, -1.48) * mm, v(-5.4, -1.6) * mm, v(-5.1, -1.53) * mm, v(-4.87, -1.35) * mm, v(-4.56, -0.78) * mm, v(-4.5, -0.36) * mm, v(-4.11, 0.8) * mm, v(-3.72, 1.42) * mm, v(-3.72, 1.43) * mm, v(-3.4, 1.4) * mm, v(-2.42, 1.96) * mm, v(-1.3, 2.96) * mm, v(-0.5, 3.68) * mm, v(-0.49, 3.68) * mm, v(-0.58, 3.38) * mm, v(-1.36, 1.9) * mm, v(-1.45, 1.69) * mm, v(-1.36, 1.4) * mm, v(-1, 1.38) * mm, v(0, 1.94) * mm, v(0.92, 2.76) * mm, v(0.92, 2.9) * mm, v(0.85, 2.94) * mm, v(0.73, 2.91) * mm, v(0.19, 2.43) * mm, v(-0.42, 2.05) * mm, v(-0.5, 2.05) * mm, v(-0.56, 2.1) * mm, v(-0.56, 2.2) * mm, v(-0.24, 2.93) * mm, v(0.7, 4.59) * mm, v(1.43, 5.86) * mm, v(1.44, 5.89) * mm, v(1.35, 6.03) * mm, v(1.08, 6.16) * mm, v(0.87, 6.13) * mm, v(0.87, 6.1) * mm, v(0.22, 5.07) * mm, v(-1.57, 3.06) * mm, v(-2.4, 2.35) * mm, v(-2.85, 2.1) * mm, v(-3.02, 2.08) * mm, v(-3.05, 2.15) * mm, v(-3, 2.46) * mm, v(-2.67, 3.08) * mm, v(-1.66, 4.9) * mm, v(-1.13, 5.9) * mm, v(-1.12, 6) * mm, v(-1.27, 6.19) * mm, v(-1.67, 6.16) * mm, v(-2.22, 5.91) * mm, v(-3, 5.37) * mm, v(-3.43, 4.97) * mm, v(-3.48, 4.9) * mm, v(-3.5, 4.74) * mm, v(-3.41, 4.67) * mm, v(-3.35, 4.7) * mm], "construction": true});
            skFitSpline(sketch, "E55", {"points": [v(2.04, 5.21) * mm, v(2, 5.21) * mm, v(2.24, 6.09) * mm, v(2.57, 7.26) * mm, v(2.58, 7.3) * mm, v(2.67, 7.34) * mm, v(2.98, 7.35) * mm, v(3.22, 7.23) * mm, v(3.25, 7.19) * mm, v(2.68, 6.22) * mm, v(2.04, 5.21) * mm], "construction": true});
            skFitSpline(sketch, "E56", {"points": [v(3.79, 4.28) * mm, v(3.92, 4.36) * mm, v(3.97, 4.67) * mm, v(3.8, 4.93) * mm, v(3.6, 5.02) * mm, v(3.38, 4.98) * mm, v(2.84, 4.67) * mm, v(2.4, 4.19) * mm, v(2.26, 3.72) * mm, v(2.4, 3.13) * mm, v(2.62, 2.47) * mm, v(2.48, 2) * mm, v(2.27, 1.78) * mm, v(1.97, 1.8) * mm, v(1.64, 2.04) * mm, v(1.58, 2.12) * mm, v(1.5, 2.13) * mm, v(1.38, 2.06) * mm, v(1.27, 1.8) * mm, v(1.35, 1.56) * mm, v(1.7, 1.41) * mm, v(2.2, 1.54) * mm, v(2.77, 2) * mm, v(3.1, 2.8) * mm, v(3, 3.18) * mm, v(2.82, 3.7) * mm, v(2.75, 4.21) * mm, v(2.95, 4.52) * mm, v(3.37, 4.63) * mm, v(3.64, 4.48) * mm, v(3.71, 4.31) * mm, v(3.79, 4.28) * mm], "construction": true});
            skLineSegment(sketch, "E57", {"start": v(0, 0) * mm, "end": v(0, 5) * mm, "construction": true});
            skCircle(sketch, "E58", {"center": v(0, 2.5) * mm, "radius": 4.25 * mm});
            skSolve(sketch);
        }
        {
            var Q0;
            Q0 = qSketchRegion(id + "F35", true);
            var Q1;
            Q1=makeQuery(id+"F35.imprint","IMPRINT",FACE,{"disambiguationData":[TD([[makeQuery(id+"F35.imprint","IMPRINT",EDGE,{"derivedFrom":sQuery(id+"F35.wireOp",EDGE,"E55")}),-1.0]])]});
            var Q2;
            Q2=makeQuery(id+"F35.imprint","IMPRINT",FACE,{"disambiguationData":[TD([[makeQuery(id+"F35.imprint","IMPRINT",EDGE,{"derivedFrom":sQuery(id+"F35.wireOp",EDGE,"E56")}),1.0]])]});
            var Q3;
            Q3=makeQuery(id+"F35.imprint","IMPRINT",FACE,{"disambiguationData":[TD([[makeQuery(id+"F35.imprint","IMPRINT",EDGE,{"derivedFrom":sQuery(id+"F35.wireOp",EDGE,"E54")}),1.0]])]});
            var Q4;
            {var subQ0=makeQuery(id+"F16.opExtrude","SWEPT_FACE",FACE,{"disambiguationData":[OSD([sQuery(id+"F15.wireOp",EDGE,"E29")])]});var subQ1=makeQuery(id+"F14.opExtrude","SWEPT_FACE",FACE,{"disambiguationData":[OSD([sQuery(id+"F13.wireOp",EDGE,"E26")])]});var subQ2=makeQuery(id+"F14.opExtrude","SWEPT_FACE",FACE,{"disambiguationData":[OSD([sQuery(id+"F13.wireOp",EDGE,"E28")])]});var subQ3=makeQuery(id+"F14.opExtrude","SWEPT_FACE",FACE,{"disambiguationData":[OSD([sQuery(id+"F13.wireOp",EDGE,"E27")])]});var subQ4=makeQuery(id+"F9.opExtrude","SWEPT_FACE",FACE,{"disambiguationData":[OSD([sQuery(id+"F8.wireOp",EDGE,"E10")])]});var subQ5=makeQuery(id+"F18.opExtrude","SWEPT_FACE",FACE,{"disambiguationData":[OSD([sQuery(id+"F17.wireOp",EDGE,"E32")])]});var subQ6=makeQuery(id+"F18.opExtrude","SWEPT_FACE",FACE,{"disambiguationData":[OSD([sQuery(id+"F17.wireOp",EDGE,"E31")])]});var subQ7=makeQuery(id+"F9.opExtrude","SWEPT_FACE",FACE,{"disambiguationData":[OSD([sQuery(id+"F8.wireOp",EDGE,"E15")])]});var subQ8=makeQuery(id+"F14.opExtrude","SWEPT_FACE",FACE,{"disambiguationData":[OSD([sQuery(id+"F13.wireOp",EDGE,"E25")])]});var subQ9=makeQuery(id+"F14.opExtrude","SWEPT_FACE",FACE,{"disambiguationData":[OSD([sQuery(id+"F13.wireOp",EDGE,"E24")])]});var subQ10=makeQuery(id+"F18.opExtrude","SWEPT_FACE",FACE,{"disambiguationData":[OSD([sQuery(id+"F17.wireOp",EDGE,"E30")])]});var subQ11=makeQuery(id+"F9.opExtrude","SWEPT_FACE",FACE,{"disambiguationData":[OSD([sQuery(id+"F8.wireOp",EDGE,"E13")])]});var subQ12=makeQuery(id+"F14.opExtrude","SWEPT_FACE",FACE,{"disambiguationData":[OSD([sQuery(id+"F13.wireOp",EDGE,"E23")])]});var subQ13=makeQuery(id+"F14.opExtrude","SWEPT_FACE",FACE,{"disambiguationData":[OSD([sQuery(id+"F13.wireOp",EDGE,"E22")])]});var subQ14=makeQuery(id+"F9.opExtrude","SWEPT_FACE",FACE,{"disambiguationData":[OSD([sQuery(id+"F8.wireOp",EDGE,"E14")])]});var subQ15=makeQuery(id+"F12.opExtrude","SWEPT_FACE",FACE,{"disambiguationData":[OSD([sQuery(id+"F11.wireOp",EDGE,"E19")])]});var subQ16=sQuery(id+"F0.wireOp",EDGE,"E0");var subQ17=makeQuery(id+"F1.opExtrude","CAP_FACE",FACE,{"disambiguationData":[OSD([subQ16])],"isStart":false});var subQ18=makeQuery(id+"F9.opExtrude","SWEPT_FACE",FACE,{"disambiguationData":[OSD([sQuery(id+"F8.wireOp",EDGE,"E11")])]});var subQ19=makeQuery(id+"F1.opExtrude","CAP_FACE",FACE,{"disambiguationData":[OSD([subQ16])],"isStart":true});var subQ20=makeQuery(id+"F9.opExtrude","SWEPT_FACE",FACE,{"disambiguationData":[OSD([sQuery(id+"F8.wireOp",EDGE,"E12")])]});var subQ21=makeQuery(id+"F14.opExtrude","SWEPT_FACE",FACE,{"disambiguationData":[OSD([sQuery(id+"F13.wireOp",EDGE,"E21")])]});var subQ22=makeQuery(id+"F12.opExtrude","SWEPT_FACE",FACE,{"disambiguationData":[OSD([sQuery(id+"F11.wireOp",EDGE,"E20")])]});var subQ23=makeQuery(id+"F18.opExtrude","SWEPT_FACE",FACE,{"disambiguationData":[OSD([sQuery(id+"F17.wireOp",EDGE,"E33")])]});var subQ24=makeQuery(id+"F18.opExtrude","SWEPT_FACE",FACE,{"disambiguationData":[OSD([sQuery(id+"F17.wireOp",EDGE,"E34")])]});var subQ25=makeQuery(id+"F18.opExtrude","SWEPT_FACE",FACE,{"disambiguationData":[OSD([sQuery(id+"F17.wireOp",EDGE,"E35")])]});Q4=makeQuery(id+"F33.boolean.opBoolean","SPLIT",FACE,{"disambiguationData":[TD([subQ19])],"derivedFrom":makeQuery(id+"F18.boolean.opBoolean","SPLIT",FACE,{"disambiguationData":[TD([subQ19,subQ17,subQ4,subQ18,subQ20,subQ11,subQ14,subQ7,subQ15,subQ22,subQ21,subQ13,subQ12,subQ9,subQ8,subQ1,subQ3,subQ2,subQ0,subQ10,subQ6,subQ5,subQ23,subQ24,subQ25])],"derivedFrom":makeQuery(id+"F16.boolean.opBoolean","SPLIT",FACE,{"disambiguationData":[TD([subQ19,subQ17,subQ4,subQ18,subQ20,subQ11,subQ14,subQ7,subQ15,subQ22,subQ21,subQ13,subQ12,subQ9,subQ8,subQ1,subQ3,subQ2,subQ0])],"derivedFrom":makeQuery(id+"F14.boolean.opBoolean","SPLIT",FACE,{"disambiguationData":[TD([subQ19,subQ17,subQ4,subQ18,subQ20,subQ11,subQ14,subQ7,subQ15,subQ22,subQ21,subQ13,subQ12,subQ9,subQ8,subQ1,subQ3,subQ2])],"derivedFrom":makeQuery(id+"F9.boolean.opBoolean","SPLIT",FACE,{"disambiguationData":[TD([subQ19])],"derivedFrom":makeQuery(id+"F1.opExtrude","SWEPT_FACE",FACE,{"disambiguationData":[OSD([subQ16])]})})})})})});}
            extrude(context, id + "F36", {"entities" : qUnion([Q0, Q1, Q2, Q3]), "operationType" : NewBodyOperationType.ADD, "endBound" : BoundingType.UP_TO_SURFACE, "oppositeDirection" : true, "depth" : 25 * mm, "endBoundEntityFace" : qUnion([Q4]), "hasOffset" : true, "offsetDistance" : 1.5 * mm, "offsetOppositeDirection" : true});
        }
        {
            var Q0;
            Q0=sQuery(id+"F2.wireOp",EDGE,"E2");
            cPoint(context, id + "F37", {"entities" : qUnion([Q0]), "parameter" : 0.5});
        }
        {
            var Q0;
            Q0=sQuery(id+"F2.wireOp",EDGE,"E1.6");
            var Q1;
            Q1 = qCreatedBy(id + "F37" ,VERTEX);
            cPlane(context, id + "F38", {"entities" : qUnion([Q0, Q1]), "cplaneType" : CPlaneType.LINE_ANGLE, "offset" : 25 * mm, "angle" : 90 * degree, "width" : 150 * mm, "height" : 150 * mm});
        }
        {
            var Q0;
            Q0=qCreatedBy(id+"F38.planeOp",FACE);
            var sketch = newSketch(context, id + "F39", { "sketchPlane" : qUnion([Q0])});
            skFitSpline(sketch, "E59", {"points": [v(0.44, 1.13) * mm, v(1.02, 1.54) * mm, v(1.16, 2.41) * mm, v(0.66, 2.58) * mm, v(0, 2.2) * mm, v(-0.48, 1.28) * mm, v(-0.38, 0.5) * mm, v(0.18, 0.23) * mm, v(1.32, 0.71) * mm, v(2.02, 1.81) * mm, v(2.16, 2.62) * mm, v(1.9, 2.93) * mm, v(1.61, 2.94) * mm], "startDerivative": vector(7.98, 3.47) * mm, "endDerivative": vector(-4.67, -1.48) * mm});
            skFitSpline(sketch, "E60", {"points": [v(0.44, 1.13) * mm, v(0.36, 1.17) * mm, v(0.75, 1.53) * mm, v(1.02, 2.2) * mm, v(0.8, 2.33) * mm, v(0.2, 1.86) * mm, v(-0.12, 1.13) * mm, v(-0.14, 0.57) * mm, v(0.17, 0.42) * mm, v(1.03, 1) * mm, v(1.54, 1.88) * mm, v(1.7, 2.53) * mm, v(1.44, 2.79) * mm, v(1, 2.83) * mm, v(0.95, 2.86) * mm], "startDerivative": vector(-3.63, 1.5) * mm, "endDerivative": vector(-1.28, 1.7) * mm});
            skFitSpline(sketch, "E61", {"points": [v(0.95, 2.86) * mm, v(1.48, 3.06) * mm, v(2.04, 3.6) * mm, v(2.23, 4.16) * mm, v(2, 4.49) * mm, v(1.49, 4.44) * mm, v(1, 3.93) * mm, v(0.9, 3.47) * mm, v(1.07, 3.27) * mm, v(1.47, 3.44) * mm, v(1.48, 3.46) * mm, v(1.41, 3.67) * mm, v(1.7, 3.84) * mm, v(1.84, 3.73) * mm, v(1.77, 3.5) * mm, v(1.53, 3.28) * mm, v(1.07, 3.1) * mm, v(0.75, 3.18) * mm, v(0.58, 3.53) * mm, v(0.69, 4.1) * mm, v(1.24, 4.65) * mm, v(1.9, 4.74) * mm, v(2.29, 4.53) * mm, v(2.52, 4.17) * mm, v(2.48, 3.65) * mm, v(2.11, 3.15) * mm, v(1.76, 2.99) * mm, v(1.6, 2.94) * mm], "startDerivative": vector(12.17, 3.2) * mm, "endDerivative": vector(-5.97, -1.92) * mm});
            skSolve(sketch);
        }
        {
            var Q0;
            Q0 = qSketchRegion(id + "F39", true);
            extrude(context, id + "F40", {"entities" : qUnion([Q0]), "operationType" : NewBodyOperationType.ADD, "oppositeDirection" : true, "depth" : 25 * mm, "offsetDistance" : 25 * mm});
        }
        {
            var Q0;
            Q0=makeQuery(id+"F10.imprint","IMPRINT",FACE,{"disambiguationData":[TD([[makeQuery(id+"F10.imprint","IMPRINT",EDGE,{"derivedFrom":sQuery(id+"F10.wireOp",EDGE,"E17")}),1.0]])]});
            var Q1;
            Q1=makeQuery(id+"F10.imprint","IMPRINT",FACE,{"disambiguationData":[TD([[makeQuery(id+"F10.imprint","IMPRINT",EDGE,{"derivedFrom":sQuery(id+"F10.wireOp",EDGE,"E18")}),-1.0]])]});
            extrude(context, id + "F41", {"entities" : qUnion([Q0, Q1]), "operationType" : NewBodyOperationType.INTERSECT, "endBound" : BoundingType.THROUGH_ALL, "oppositeDirection" : true, "depth" : 25 * mm, "offsetDistance" : 25 * mm, "hasSecondDirection" : true, "secondDirectionBound" : SecondDirectionBoundingType.THROUGH_ALL, "secondDirectionOppositeDirection" : false, "secondDirectionDepth" : 25 * mm});
        }
        {
            var Q0;
            Q0=makeQuery(id+"F1.opExtrude","CAP_FACE",FACE,{"disambiguationData":[OSD([sQuery(id+"F0.wireOp",EDGE,"E0")])],"isStart":false});
            var sketch = newSketch(context, id + "F42", { "sketchPlane" : qUnion([Q0])});
            skCircle(sketch, "E62", {"center": v(0, 0) * mm, "radius": 7.5 * mm});
            skCircle(sketch, "E63", {"center": v(0, 0) * mm, "radius": 9 * mm});
            skSolve(sketch);
        }
        {
            var Q0;
            Q0 = qSketchRegion(id + "F42", true);
            extrude(context, id + "F43", {"entities" : qUnion([Q0]), "operationType" : NewBodyOperationType.ADD, "depth" : 0.75 * mm, "offsetDistance" : 25 * mm});
        }
        {
            var Q0;
            Q0=makeQuery(id+"F1.opExtrude","CAP_FACE",FACE,{"disambiguationData":[OSD([sQuery(id+"F0.wireOp",EDGE,"E0")])],"isStart":true});
            var sketch = newSketch(context, id + "F44", { "sketchPlane" : qUnion([Q0])});
            skCircle(sketch, "E64.0", {"center": v(0, 0) * mm, "radius": 7.5 * mm});
            skCircle(sketch, "E65", {"center": v(0, 0) * mm, "radius": 9 * mm});
            skSolve(sketch);
        }
        {
            var Q0;
            Q0 = qSketchRegion(id + "F44", true);
            extrude(context, id + "F45", {"entities" : qUnion([Q0]), "operationType" : NewBodyOperationType.ADD, "depth" : 0.75 * mm, "offsetDistance" : 25 * mm});
        }
        {
            var Q0;
            Q0=sQuery(id+"F2.wireOp",EDGE,"E9");
            var Q1;
            Q1=sQuery(id+"F2.wireOp",VERTEX,"E3.start");
            cPlane(context, id + "F46", {"entities" : qUnion([Q0, Q1]), "cplaneType" : CPlaneType.LINE_ANGLE, "offset" : 25 * mm, "angle" : 90 * degree, "width" : 150 * mm, "height" : 150 * mm});
        }
        {
            var Q0;
            Q0=qCreatedBy(id+"F46.planeOp",FACE);
            var sketch = newSketch(context, id + "F47", { "sketchPlane" : qUnion([Q0])});
            skLineSegment(sketch, "E66.bottom", {"start": v(1, -0.75) * mm, "end": v(-1, -0.75) * mm});
            skLineSegment(sketch, "E66.top", {"start": v(1, 5.75) * mm, "end": v(-1, 5.75) * mm});
            skLineSegment(sketch, "E66.left", {"start": v(1, -0.75) * mm, "end": v(1, 5.75) * mm});
            skLineSegment(sketch, "E66.right", {"start": v(-1, -0.75) * mm, "end": v(-1, 5.75) * mm});
            skPoint(sketch, "E66.middle", {"position": v(0, 2.5) * mm});
            skSolve(sketch);
        }
        {
            var Q0;
            Q0 = qSketchRegion(id + "F47", true);
            var Q1;
            {var subQ0=makeQuery(id+"F16.opExtrude","SWEPT_FACE",FACE,{"disambiguationData":[OSD([sQuery(id+"F15.wireOp",EDGE,"E29")])]});var subQ1=makeQuery(id+"F14.opExtrude","SWEPT_FACE",FACE,{"disambiguationData":[OSD([sQuery(id+"F13.wireOp",EDGE,"E26")])]});var subQ2=makeQuery(id+"F14.opExtrude","SWEPT_FACE",FACE,{"disambiguationData":[OSD([sQuery(id+"F13.wireOp",EDGE,"E24")])]});var subQ3=makeQuery(id+"F18.opExtrude","SWEPT_FACE",FACE,{"disambiguationData":[OSD([sQuery(id+"F17.wireOp",EDGE,"E30")])]});var subQ4=makeQuery(id+"F14.opExtrude","SWEPT_FACE",FACE,{"disambiguationData":[OSD([sQuery(id+"F13.wireOp",EDGE,"E23")])]});var subQ5=makeQuery(id+"F14.opExtrude","SWEPT_FACE",FACE,{"disambiguationData":[OSD([sQuery(id+"F13.wireOp",EDGE,"E21")])]});var subQ6=makeQuery(id+"F14.opExtrude","SWEPT_FACE",FACE,{"disambiguationData":[OSD([sQuery(id+"F13.wireOp",EDGE,"E22")])]});var subQ7=makeQuery(id+"F9.opExtrude","SWEPT_FACE",FACE,{"disambiguationData":[OSD([sQuery(id+"F8.wireOp",EDGE,"E10")])]});var subQ8=makeQuery(id+"F14.opExtrude","SWEPT_FACE",FACE,{"disambiguationData":[OSD([sQuery(id+"F13.wireOp",EDGE,"E28")])]});var subQ9=makeQuery(id+"F9.opExtrude","SWEPT_FACE",FACE,{"disambiguationData":[OSD([sQuery(id+"F8.wireOp",EDGE,"E14")])]});var subQ10=makeQuery(id+"F18.opExtrude","SWEPT_FACE",FACE,{"disambiguationData":[OSD([sQuery(id+"F17.wireOp",EDGE,"E31")])]});var subQ11=makeQuery(id+"F14.opExtrude","SWEPT_FACE",FACE,{"disambiguationData":[OSD([sQuery(id+"F13.wireOp",EDGE,"E25")])]});var subQ12=makeQuery(id+"F9.opExtrude","SWEPT_FACE",FACE,{"disambiguationData":[OSD([sQuery(id+"F8.wireOp",EDGE,"E11")])]});var subQ13=sQuery(id+"F0.wireOp",EDGE,"E0");var subQ14=makeQuery(id+"F1.opExtrude","CAP_FACE",FACE,{"disambiguationData":[OSD([subQ13])],"isStart":true});var subQ15=makeQuery(id+"F18.opExtrude","SWEPT_FACE",FACE,{"disambiguationData":[OSD([sQuery(id+"F17.wireOp",EDGE,"E35")])]});var subQ16=makeQuery(id+"F14.opExtrude","SWEPT_FACE",FACE,{"disambiguationData":[OSD([sQuery(id+"F13.wireOp",EDGE,"E27")])]});var subQ17=makeQuery(id+"F9.opExtrude","SWEPT_FACE",FACE,{"disambiguationData":[OSD([sQuery(id+"F8.wireOp",EDGE,"E13")])]});var subQ18=makeQuery(id+"F18.opExtrude","SWEPT_FACE",FACE,{"disambiguationData":[OSD([sQuery(id+"F17.wireOp",EDGE,"E32")])]});var subQ19=makeQuery(id+"F1.opExtrude","CAP_FACE",FACE,{"disambiguationData":[OSD([subQ13])],"isStart":false});var subQ20=makeQuery(id+"F9.opExtrude","SWEPT_FACE",FACE,{"disambiguationData":[OSD([sQuery(id+"F8.wireOp",EDGE,"E12")])]});var subQ21=makeQuery(id+"F12.opExtrude","SWEPT_FACE",FACE,{"disambiguationData":[OSD([sQuery(id+"F11.wireOp",EDGE,"E20")])]});var subQ22=makeQuery(id+"F9.opExtrude","SWEPT_FACE",FACE,{"disambiguationData":[OSD([sQuery(id+"F8.wireOp",EDGE,"E15")])]});var subQ23=makeQuery(id+"F12.opExtrude","SWEPT_FACE",FACE,{"disambiguationData":[OSD([sQuery(id+"F11.wireOp",EDGE,"E19")])]});var subQ24=makeQuery(id+"F18.opExtrude","SWEPT_FACE",FACE,{"disambiguationData":[OSD([sQuery(id+"F17.wireOp",EDGE,"E33")])]});var subQ25=makeQuery(id+"F18.opExtrude","SWEPT_FACE",FACE,{"disambiguationData":[OSD([sQuery(id+"F17.wireOp",EDGE,"E34")])]});Q1=makeQuery(id+"F33.boolean.opBoolean","SPLIT",FACE,{"disambiguationData":[TD([subQ14])],"derivedFrom":makeQuery(id+"F18.boolean.opBoolean","SPLIT",FACE,{"disambiguationData":[TD([subQ14,subQ19,subQ7,subQ12,subQ20,subQ17,subQ9,subQ22,subQ23,subQ21,subQ5,subQ6,subQ4,subQ2,subQ11,subQ1,subQ16,subQ8,subQ0,subQ3,subQ10,subQ18,subQ24,subQ25,subQ15])],"derivedFrom":makeQuery(id+"F16.boolean.opBoolean","SPLIT",FACE,{"disambiguationData":[TD([subQ14,subQ19,subQ7,subQ12,subQ20,subQ17,subQ9,subQ22,subQ23,subQ21,subQ5,subQ6,subQ4,subQ2,subQ11,subQ1,subQ16,subQ8,subQ0])],"derivedFrom":makeQuery(id+"F14.boolean.opBoolean","SPLIT",FACE,{"disambiguationData":[TD([subQ14,subQ19,subQ7,subQ12,subQ20,subQ17,subQ9,subQ22,subQ23,subQ21,subQ5,subQ6,subQ4,subQ2,subQ11,subQ1,subQ16,subQ8])],"derivedFrom":makeQuery(id+"F9.boolean.opBoolean","SPLIT",FACE,{"disambiguationData":[TD([subQ14])],"derivedFrom":makeQuery(id+"F1.opExtrude","SWEPT_FACE",FACE,{"disambiguationData":[OSD([subQ13])]})})})})})});}
            extrude(context, id + "F48", {"entities" : qUnion([Q0]), "operationType" : NewBodyOperationType.ADD, "endBound" : BoundingType.UP_TO_SURFACE, "oppositeDirection" : true, "depth" : 25 * mm, "endBoundEntityFace" : qUnion([Q1]), "offsetDistance" : 25 * mm});
        }
        {
            var Q0;
            Q0=makeQuery(id+"F48.boolean.opBoolean","MERGE",FACE,{"derivedFrom":[makeQuery(id+"F43.opExtrude","CAP_FACE",FACE,{"disambiguationData":[OSD([sQuery(id+"F42.wireOp",EDGE,"619114e6-78bb-48f3-b0c1-2d6fb18d54e1.0"),sQuery(id+"F42.wireOp",EDGE,"062b4c25-6b0a-4cbd-93e0-bf44892a4fa7.0")])],"isStart":false}),makeQuery(id+"F48.opExtrude","SWEPT_FACE",FACE,{"disambiguationData":[OSD([sQuery(id+"F47.wireOp",EDGE,"E66.top")])]})]});
            var sketch = newSketch(context, id + "F49", { "sketchPlane" : qUnion([Q0])});
            skArc(sketch, "E67", {"start": v(-5.83, -6.86) * mm, "mid": v(-5.03, -7.46) * mm, "end": v(-4.17, -7.98) * mm});
            skLineSegment(sketch, "E68.0", {"start": v(-4.17, -7.98) * mm, "end": v(-14.36, -23.11) * mm});
            skLineSegment(sketch, "E68.1", {"start": v(-5.83, -6.86) * mm, "end": v(-16.02, -22) * mm});
            skLineSegment(sketch, "E68.2", {"start": v(-14.36, -23.11) * mm, "end": v(-16.02, -22) * mm});
            skLineSegment(sketch, "E69", {"start": v(-4.9, -7.55) * mm, "end": v(0, 0) * mm});
            skLineSegment(sketch, "E70", {"start": v(-5.16, -7.38) * mm, "end": v(0, 0) * mm});
            skSolve(sketch);
        }
        {
            var Q0;
            Q0 = qSketchRegion(id + "F49", true);
            extrude(context, id + "F50", {"entities" : qUnion([Q0]), "operationType" : NewBodyOperationType.REMOVE, "endBound" : BoundingType.THROUGH_ALL, "oppositeDirection" : true, "depth" : 25 * mm, "offsetDistance" : 25 * mm});
        }
        {
            var Q0;
            Q0=makeQuery(id+"F48.boolean.opBoolean","INTERSECT",EDGE,{"derivedFrom":[makeQuery(id+"F43.opExtrude","CAP_FACE",FACE,{"disambiguationData":[OSD([sQuery(id+"F42.wireOp",EDGE,"619114e6-78bb-48f3-b0c1-2d6fb18d54e1.0"),sQuery(id+"F42.wireOp",EDGE,"062b4c25-6b0a-4cbd-93e0-bf44892a4fa7.0")])],"isStart":true}),makeQuery(id+"F48.opExtrude","SWEPT_FACE",FACE,{"disambiguationData":[OSD([sQuery(id+"F47.wireOp",EDGE,"E66.right")])]})]});
            var Q1;
            Q1=makeQuery(id+"F48.boolean.opBoolean","INTERSECT",EDGE,{"derivedFrom":[makeQuery(id+"F45.opExtrude","CAP_FACE",FACE,{"disambiguationData":[OSD([sQuery(id+"F44.wireOp",EDGE,"36ce2d2d-1cae-423c-bb2f-8b0e1f9c5fca.0.0"),sQuery(id+"F44.wireOp",EDGE,"E64.0")])],"isStart":true}),makeQuery(id+"F48.opExtrude","SWEPT_FACE",FACE,{"disambiguationData":[OSD([sQuery(id+"F47.wireOp",EDGE,"E66.right")])]})]});
            var Q2;
            Q2=makeQuery(id+"F48.boolean.opBoolean","INTERSECT",EDGE,{"derivedFrom":[makeQuery(id+"F43.opExtrude","CAP_FACE",FACE,{"disambiguationData":[OSD([sQuery(id+"F42.wireOp",EDGE,"619114e6-78bb-48f3-b0c1-2d6fb18d54e1.0"),sQuery(id+"F42.wireOp",EDGE,"062b4c25-6b0a-4cbd-93e0-bf44892a4fa7.0")])],"isStart":true}),makeQuery(id+"F48.opExtrude","SWEPT_FACE",FACE,{"disambiguationData":[OSD([sQuery(id+"F47.wireOp",EDGE,"E66.left")])]})]});
            var Q3;
            Q3=makeQuery(id+"F48.boolean.opBoolean","INTERSECT",EDGE,{"derivedFrom":[makeQuery(id+"F45.opExtrude","CAP_FACE",FACE,{"disambiguationData":[OSD([sQuery(id+"F44.wireOp",EDGE,"36ce2d2d-1cae-423c-bb2f-8b0e1f9c5fca.0.0"),sQuery(id+"F44.wireOp",EDGE,"E64.0")])],"isStart":true}),makeQuery(id+"F48.opExtrude","SWEPT_FACE",FACE,{"disambiguationData":[OSD([sQuery(id+"F47.wireOp",EDGE,"E66.left")])]})]});
            fillet(context, id + "F51", {"entities" : qUnion([Q0, Q1, Q2, Q3]), "radius" : 1 * mm, "tangentPropagation" : true, "allowEdgeOverflow" : false});
        }
        {
            var Q0;
            Q0=makeQuery(id+"F50.boolean.opBoolean","COPY",EDGE,{"derivedFrom":makeQuery(id+"F50.opExtrude","CAP_EDGE",EDGE,{"disambiguationData":[OSD([sQuery(id+"F49.wireOp",EDGE,"E70")])],"isStart":true})});
            var Q1;
            Q1=makeQuery(id+"F50.boolean.opBoolean","INTERSECT",EDGE,{"derivedFrom":[makeQuery(id+"F48.boolean.opBoolean","MERGE",FACE,{"derivedFrom":[makeQuery(id+"F45.opExtrude","CAP_FACE",FACE,{"disambiguationData":[OSD([sQuery(id+"F44.wireOp",EDGE,"36ce2d2d-1cae-423c-bb2f-8b0e1f9c5fca.0.0"),sQuery(id+"F44.wireOp",EDGE,"E64.0")])],"isStart":false}),makeQuery(id+"F48.opExtrude","SWEPT_FACE",FACE,{"disambiguationData":[OSD([sQuery(id+"F47.wireOp",EDGE,"E66.bottom")])]})]}),makeQuery(id+"F50.opExtrude","SWEPT_FACE",FACE,{"disambiguationData":[OSD([sQuery(id+"F49.wireOp",EDGE,"E70")])]})]});
            var Q2;
            Q2=makeQuery(id+"F50.boolean.opBoolean","INTERSECT",EDGE,{"derivedFrom":[makeQuery(id+"F48.boolean.opBoolean","MERGE",FACE,{"derivedFrom":[makeQuery(id+"F45.opExtrude","CAP_FACE",FACE,{"disambiguationData":[OSD([sQuery(id+"F44.wireOp",EDGE,"36ce2d2d-1cae-423c-bb2f-8b0e1f9c5fca.0.0"),sQuery(id+"F44.wireOp",EDGE,"E64.0")])],"isStart":false}),makeQuery(id+"F48.opExtrude","SWEPT_FACE",FACE,{"disambiguationData":[OSD([sQuery(id+"F47.wireOp",EDGE,"E66.bottom")])]})]}),makeQuery(id+"F50.opExtrude","SWEPT_FACE",FACE,{"disambiguationData":[OSD([sQuery(id+"F49.wireOp",EDGE,"E69")])]})]});
            var Q3;
            Q3=makeQuery(id+"F50.boolean.opBoolean","COPY",EDGE,{"derivedFrom":makeQuery(id+"F50.opExtrude","CAP_EDGE",EDGE,{"disambiguationData":[OSD([sQuery(id+"F49.wireOp",EDGE,"E69")])],"isStart":true})});
            fillet(context, id + "F52", {"entities" : qUnion([Q0, Q1, Q2, Q3]), "radius" : 1.5 * mm, "tangentPropagation" : true, "allowEdgeOverflow" : false});
        }
        {
            var Q0;
            Q0=qCreatedBy(id+"F34.planeOp",FACE);
            var sketch = newSketch(context, id + "F53", { "sketchPlane" : qUnion([Q0])});
            skFitSpline(sketch, "E71", {"points": [v(-2.42, 1.7) * mm, v(-2.01, 1.75) * mm, v(-1.24, 2.2) * mm, v(-0.55, 2.92) * mm, v(0.13, 3.76) * mm, v(0.13, 3.74) * mm, v(0.06, 3.45) * mm, v(-0.45, 2.3) * mm, v(-0.55, 2.06) * mm, v(-0.48, 1.84) * mm, v(-0.31, 1.78) * mm, v(0, 1.89) * mm, v(0.64, 2.34) * mm, v(1.36, 3.08) * mm, v(1.34, 3.21) * mm, v(1.24, 3.22) * mm, v(1.06, 3.05) * mm, v(0.5, 2.56) * mm, v(0.26, 2.42) * mm, v(0.17, 2.44) * mm, v(0.17, 2.51) * mm, v(0.34, 3.04) * mm, v(0.89, 4.2) * mm, v(1.3, 5) * mm, v(1.6, 5.65) * mm, v(1.61, 5.7) * mm, v(1.6, 5.74) * mm, v(1.49, 5.87) * mm, v(1.32, 5.92) * mm, v(1.14, 5.9) * mm, v(1.13, 5.87) * mm, v(0.98, 5.53) * mm, v(0.06, 4.24) * mm, v(-0.92, 3.08) * mm, v(-1.52, 2.51) * mm, v(-1.8, 2.3) * mm, v(-1.87, 2.3) * mm, v(-1.89, 2.33) * mm, v(-1.9, 2.57) * mm, v(-1.86, 2.65) * mm, v(-0.99, 4.5) * mm, v(-0.52, 5.57) * mm, v(-0.54, 5.68) * mm, v(-0.68, 5.81) * mm, v(-1, 5.76) * mm, v(-1.51, 5.48) * mm, v(-2, 5.06) * mm, v(-2.39, 4.64) * mm, v(-2.43, 4.52) * mm, v(-2.4, 4.45) * mm, v(-2.34, 4.43) * mm, v(-2.18, 4.58) * mm, v(-1.79, 4.93) * mm, v(-1.49, 5.1) * mm, v(-1.38, 5.11) * mm, v(-1.35, 5.05) * mm, v(-1.4, 4.94) * mm, v(-2.3, 2.96) * mm, v(-3.28, 0.77) * mm, v(-3.3, 0.73) * mm, v(-3.13, 0.3) * mm, v(-2.76, -0.09) * mm, v(-2.72, -0.06) * mm, v(-2.85, 0.4) * mm, v(-2.88, 0.54) * mm, v(-2.73, 1.08) * mm, v(-2.47, 1.65) * mm, v(-2.42, 1.7) * mm]});
            skFitSpline(sketch, "E72", {"points": [v(1.8, 3.42) * mm, v(2.3, 4.35) * mm, v(2.68, 5.12) * mm, v(2.67, 5.18) * mm, v(2.61, 5.24) * mm, v(2.44, 5.28) * mm, v(2.25, 5.27) * mm, v(2.15, 5.2) * mm, v(2.13, 5.15) * mm, v(1.85, 3.78) * mm, v(1.8, 3.42) * mm]});
            skFitSpline(sketch, "E73", {"points": [v(3.06, 2.77) * mm, v(3.15, 2.77) * mm, v(3.23, 2.92) * mm, v(3.22, 3.16) * mm, v(3.02, 3.35) * mm, v(2.83, 3.36) * mm, v(2.34, 3.21) * mm, v(1.94, 2.8) * mm, v(1.8, 2.5) * mm, v(1.8, 2.24) * mm, v(1.9, 2) * mm, v(2.06, 1.63) * mm, v(2.22, 1.3) * mm, v(2.21, 0.94) * mm, v(2.08, 0.68) * mm, v(1.9, 0.58) * mm, v(1.7, 0.61) * mm, v(1.48, 0.76) * mm, v(1.4, 0.85) * mm, v(1.34, 0.85) * mm, v(1.28, 0.83) * mm, v(1.18, 0.73) * mm, v(1.16, 0.54) * mm, v(1.2, 0.4) * mm, v(1.36, 0.3) * mm, v(1.58, 0.27) * mm, v(1.96, 0.36) * mm, v(2.39, 0.68) * mm, v(2.58, 1.14) * mm, v(2.63, 1.4) * mm, v(2.6, 1.68) * mm, v(2.47, 1.92) * mm, v(2.3, 2.34) * mm, v(2.26, 2.63) * mm, v(2.3, 2.8) * mm, v(2.49, 2.97) * mm, v(2.68, 3.02) * mm, v(2.88, 3) * mm, v(3, 2.87) * mm, v(3.04, 2.8) * mm, v(3.06, 2.77) * mm]});
            skSolve(sketch);
        }
        {
            var Q0;
            Q0 = qSketchRegion(id + "F53", true);
            var Q1;
            {var subQ0=sQuery(id+"F49.wireOp",EDGE,"E67");var subQ1=sQuery(id+"F42.wireOp",EDGE,"E63");var subQ2=makeQuery(id+"F43.opExtrude","SWEPT_FACE",FACE,{"disambiguationData":[OSD([subQ1])]});var subQ4=makeQuery(id+"F36.opExtrude","SWEPT_FACE",FACE,{"disambiguationData":[OSD([sQuery(id+"F35.wireOp",EDGE,"E58")])]});var subQ5=makeQuery(id+"F41.boolean.opBoolean","COPY",FACE,{"disambiguationData":[TD([subQ4])],"derivedFrom":makeQuery(id+"F41.boolean.toolComplement.opBoolean","COPY",FACE,{"derivedFrom":makeQuery(id+"F41.opExtrude","SWEPT_FACE",FACE,{"disambiguationData":[OSD([sQuery(id+"F10.wireOp",EDGE,"E17")])]})})});var subQ6=makeQuery(id+"F45.opExtrude","SWEPT_FACE",FACE,{"disambiguationData":[OSD([sQuery(id+"F44.wireOp",EDGE,"E65")])]});Q1=makeQuery(id+"F50.boolean.opBoolean","MERGE",FACE,{"derivedFrom":[makeQuery(id+"F45.boolean.opBoolean","MERGE",FACE,{"derivedFrom":[makeQuery(id+"F43.boolean.opBoolean","MERGE",FACE,{"derivedFrom":[subQ5,subQ2]}),subQ6]})],"fromTools":[makeQuery(id+"F50.opExtrude","SWEPT_FACE",FACE,{"disambiguationData":[OSD([subQ0]),TDD([makeQuery(id+"F49.imprint","IMPRINT",EDGE,{"disambiguationData":[TD([[makeQuery(id+"F49.imprint","INTERSECT",VERTEX,{"derivedFrom":[subQ0,sQuery(id+"F49.wireOp",EDGE,"E70")]}),1.0]])],"derivedFrom":subQ0})])]}),makeQuery(id+"F50.opExtrude","SWEPT_FACE",FACE,{"disambiguationData":[OSD([subQ0]),TDD([makeQuery(id+"F49.imprint","IMPRINT",EDGE,{"disambiguationData":[TD([[makeQuery(id+"F49.imprint","INTERSECT",VERTEX,{"derivedFrom":[subQ0,sQuery(id+"F49.wireOp",EDGE,"E69")]}),-1.0]])],"derivedFrom":subQ0})])]})]});}
            extrude(context, id + "F54", {"entities" : qUnion([Q0]), "operationType" : NewBodyOperationType.REMOVE, "endBound" : BoundingType.UP_TO_SURFACE, "oppositeDirection" : true, "depth" : 25 * mm, "endBoundEntityFace" : qUnion([Q1]), "hasOffset" : true, "offsetDistance" : 0.5 * mm, "offsetOppositeDirection" : true});
        }
        {
            var Q0;
            Q0=makeQuery(id+"F43.boolean.opBoolean","INTERSECT",EDGE,{"disambiguationData":[OD(0.0)],"derivedFrom":[makeQuery(id+"F36.opExtrude","SWEPT_FACE",FACE,{"disambiguationData":[OSD([sQuery(id+"F35.wireOp",EDGE,"E58")])]}),makeQuery(id+"F43.opExtrude","CAP_FACE",FACE,{"disambiguationData":[OSD([sQuery(id+"F42.wireOp",EDGE,"E62"),sQuery(id+"F42.wireOp",EDGE,"E63")])],"isStart":false})]});
            var Q1;
            Q1=makeQuery(id+"F43.boolean.opBoolean","INTERSECT",EDGE,{"disambiguationData":[OD(1.0)],"derivedFrom":[makeQuery(id+"F36.opExtrude","SWEPT_FACE",FACE,{"disambiguationData":[OSD([sQuery(id+"F35.wireOp",EDGE,"E58")])]}),makeQuery(id+"F43.opExtrude","CAP_FACE",FACE,{"disambiguationData":[OSD([sQuery(id+"F42.wireOp",EDGE,"E62"),sQuery(id+"F42.wireOp",EDGE,"E63")])],"isStart":false})]});
            var Q2;
            {var subQ0=makeQuery(id+"F36.opExtrude","SWEPT_FACE",FACE,{"disambiguationData":[OSD([sQuery(id+"F35.wireOp",EDGE,"E58")])]});var subQ1=sQuery(id+"F0.wireOp",EDGE,"E0");Q2=makeQuery(id+"F45.boolean.opBoolean","INTERSECT",EDGE,{"disambiguationData":[OD(1.0)],"derivedFrom":[makeQuery(id+"F43.boolean.opBoolean","SPLIT",FACE,{"disambiguationData":[TD([makeQuery(id+"F1.opExtrude","SWEPT_FACE",FACE,{"disambiguationData":[OSD([subQ1])]})])],"derivedFrom":subQ0}),makeQuery(id+"F45.opExtrude","CAP_FACE",FACE,{"disambiguationData":[OSD([sQuery(id+"F44.wireOp",EDGE,"E64.0"),sQuery(id+"F44.wireOp",EDGE,"E65")])],"isStart":false})]});}
            var Q3;
            {var subQ0=makeQuery(id+"F36.opExtrude","SWEPT_FACE",FACE,{"disambiguationData":[OSD([sQuery(id+"F35.wireOp",EDGE,"E58")])]});var subQ1=sQuery(id+"F0.wireOp",EDGE,"E0");Q3=makeQuery(id+"F45.boolean.opBoolean","INTERSECT",EDGE,{"disambiguationData":[OD(0.0)],"derivedFrom":[makeQuery(id+"F43.boolean.opBoolean","SPLIT",FACE,{"disambiguationData":[TD([makeQuery(id+"F1.opExtrude","SWEPT_FACE",FACE,{"disambiguationData":[OSD([subQ1])]})])],"derivedFrom":subQ0}),makeQuery(id+"F45.opExtrude","CAP_FACE",FACE,{"disambiguationData":[OSD([sQuery(id+"F44.wireOp",EDGE,"E64.0"),sQuery(id+"F44.wireOp",EDGE,"E65")])],"isStart":false})]});}
            var Q4;
            {var subQ0=makeQuery(id+"F36.opExtrude","SWEPT_FACE",FACE,{"disambiguationData":[OSD([sQuery(id+"F35.wireOp",EDGE,"E58")])]});var subQ1=sQuery(id+"F0.wireOp",EDGE,"E0");Q4=makeQuery(id+"F45.boolean.opBoolean","INTERSECT",EDGE,{"disambiguationData":[OD(0.0)],"derivedFrom":[makeQuery(id+"F43.boolean.opBoolean","SPLIT",FACE,{"disambiguationData":[TD([makeQuery(id+"F1.opExtrude","SWEPT_FACE",FACE,{"disambiguationData":[OSD([subQ1])]})])],"derivedFrom":subQ0}),makeQuery(id+"F45.opExtrude","CAP_FACE",FACE,{"disambiguationData":[OSD([sQuery(id+"F44.wireOp",EDGE,"E64.0"),sQuery(id+"F44.wireOp",EDGE,"E65")])],"isStart":true})]});}
            var Q5;
            Q5=makeQuery(id+"F43.boolean.opBoolean","INTERSECT",EDGE,{"disambiguationData":[OD(0.0)],"derivedFrom":[makeQuery(id+"F36.opExtrude","SWEPT_FACE",FACE,{"disambiguationData":[OSD([sQuery(id+"F35.wireOp",EDGE,"E58")])]}),makeQuery(id+"F43.opExtrude","CAP_FACE",FACE,{"disambiguationData":[OSD([sQuery(id+"F42.wireOp",EDGE,"E62"),sQuery(id+"F42.wireOp",EDGE,"E63")])],"isStart":true})]});
            var Q6;
            Q6=makeQuery(id+"F43.boolean.opBoolean","INTERSECT",EDGE,{"disambiguationData":[OD(1.0)],"derivedFrom":[makeQuery(id+"F36.opExtrude","SWEPT_FACE",FACE,{"disambiguationData":[OSD([sQuery(id+"F35.wireOp",EDGE,"E58")])]}),makeQuery(id+"F43.opExtrude","CAP_FACE",FACE,{"disambiguationData":[OSD([sQuery(id+"F42.wireOp",EDGE,"E62"),sQuery(id+"F42.wireOp",EDGE,"E63")])],"isStart":true})]});
            var Q7;
            {var subQ0=makeQuery(id+"F36.opExtrude","SWEPT_FACE",FACE,{"disambiguationData":[OSD([sQuery(id+"F35.wireOp",EDGE,"E58")])]});var subQ1=sQuery(id+"F0.wireOp",EDGE,"E0");Q7=makeQuery(id+"F45.boolean.opBoolean","INTERSECT",EDGE,{"disambiguationData":[OD(1.0)],"derivedFrom":[makeQuery(id+"F43.boolean.opBoolean","SPLIT",FACE,{"disambiguationData":[TD([makeQuery(id+"F1.opExtrude","SWEPT_FACE",FACE,{"disambiguationData":[OSD([subQ1])]})])],"derivedFrom":subQ0}),makeQuery(id+"F45.opExtrude","CAP_FACE",FACE,{"disambiguationData":[OSD([sQuery(id+"F44.wireOp",EDGE,"E64.0"),sQuery(id+"F44.wireOp",EDGE,"E65")])],"isStart":true})]});}
            fillet(context, id + "F55", {"entities" : qUnion([Q0, Q1, Q2, Q3, Q4, Q5, Q6, Q7]), "radius" : 1 * mm, "tangentPropagation" : true, "allowEdgeOverflow" : false});
        }
        {
            var Q0;
            {var subQ0=makeQuery(id+"F36.opExtrude","SWEPT_FACE",FACE,{"disambiguationData":[OSD([sQuery(id+"F35.wireOp",EDGE,"E58")])]});var subQ1=makeQuery(id+"F41.boolean.toolComplement.opBoolean","COPY",FACE,{"derivedFrom":makeQuery(id+"F41.opExtrude","SWEPT_FACE",FACE,{"disambiguationData":[OSD([sQuery(id+"F10.wireOp",EDGE,"E17")])]})});var subQ2=sQuery(id+"F42.wireOp",EDGE,"E63");Q0=makeQuery(id+"F43.boolean.opBoolean","SPLIT",EDGE,{"disambiguationData":[TD([makeQuery(id+"F43.opExtrude","CAP_FACE",FACE,{"disambiguationData":[OSD([sQuery(id+"F42.wireOp",EDGE,"E62"),subQ2])],"isStart":false})])],"derivedFrom":makeQuery(id+"F41.boolean.opBoolean","INTERSECT",EDGE,{"derivedFrom":[subQ0,subQ1]})});}
            var Q1;
            {var subQ0=sQuery(id+"F42.wireOp",EDGE,"E62");Q1=makeQuery(id+"F50.boolean.opBoolean","SPLIT",EDGE,{"disambiguationData":[TD([makeQuery(id+"F50.opExtrude","SWEPT_FACE",FACE,{"disambiguationData":[OSD([sQuery(id+"F49.wireOp",EDGE,"E69")])]})])],"derivedFrom":makeQuery(id+"F43.opExtrude","CAP_EDGE",EDGE,{"disambiguationData":[OSD([subQ0])],"isStart":false})});}
            fillet(context, id + "F56", {"entities" : qUnion([Q0, Q1]), "radius" : 0.5 * mm, "tangentPropagation" : true, "allowEdgeOverflow" : false});
        }
    });
